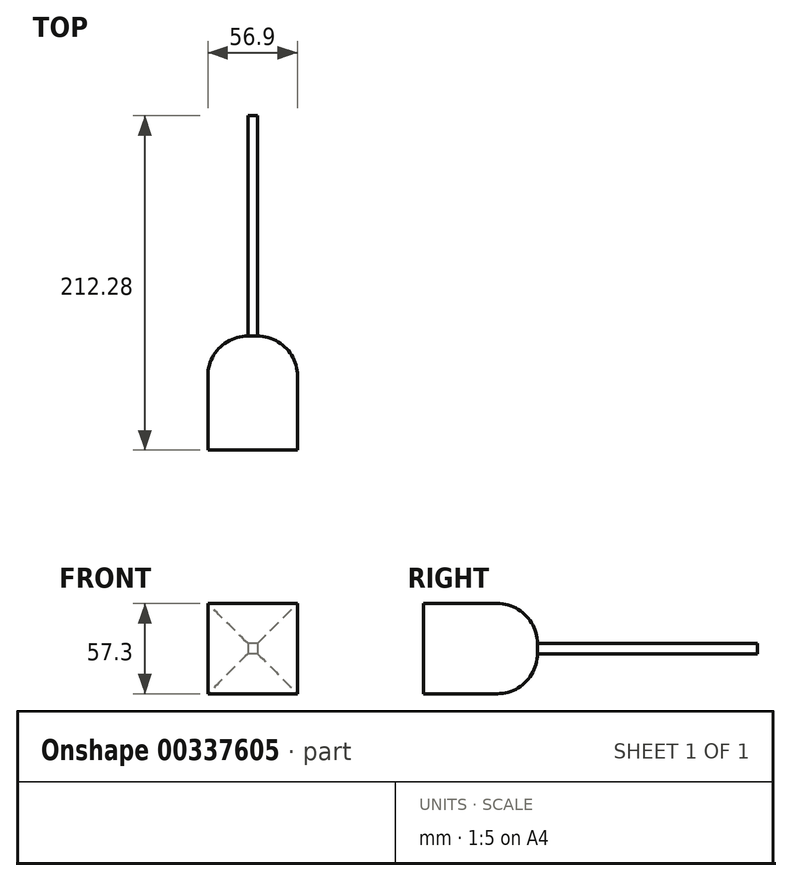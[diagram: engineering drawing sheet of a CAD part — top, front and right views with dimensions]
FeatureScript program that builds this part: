
annotation { "Feature Type Name" : "Feature", "Feature Type Description" : "" }
export const myFeature = defineFeature(function(context is Context, id is Id, definition is map)
    precondition{}
    {
        {
            var Q0;
            Q0=qCreatedBy(makeId("Top.planeOp"),FACE);
            var sketch = newSketch(context, id + "F0", { "sketchPlane" : qUnion([Q0])});
            skLineSegment(sketch, "E0.bottom", {"start": v(0, 0) * mm, "end": v(0, 0) * mm});
            skLineSegment(sketch, "E0.top", {"start": v(0, 0) * mm, "end": v(0, 0) * mm});
            skLineSegment(sketch, "E0.left", {"start": v(0, 0) * mm, "end": v(0, 0) * mm});
            skLineSegment(sketch, "E0.right", {"start": v(0, 0) * mm, "end": v(0, 0) * mm});
            skLineSegment(sketch, "E1.bottom", {"start": v(56.9, -72.43) * mm, "end": v(0, -72.43) * mm});
            skLineSegment(sketch, "E1.top", {"start": v(56.9, 0) * mm, "end": v(0, 0) * mm});
            skLineSegment(sketch, "E1.left", {"start": v(56.9, -72.43) * mm, "end": v(56.9, 0) * mm});
            skLineSegment(sketch, "E1.right", {"start": v(0, -72.43) * mm, "end": v(0, 0) * mm});
            skSolve(sketch);
        }
        {
            var Q0;
            Q0=makeQuery(id+"F0.imprint","IMPRINT",FACE,{"disambiguationData":[TD([[makeQuery(id+"F0.imprint","IMPRINT",EDGE,{"derivedFrom":sQuery(id+"F0.wireOp",EDGE,"E1.bottom")}),-1.0]])]});
            extrude(context, id + "F1", {"entities" : qUnion([Q0]), "endBound" : BoundingType.SYMMETRIC, "depth" : 57.3 * mm});
        }
        {
            var Q0;
            Q0=makeQuery(id+"F1.opExtrude","SWEPT_FACE",FACE,{"disambiguationData":[OSD([sQuery(id+"F0.wireOp",EDGE,"E1.top")])]});
            fillet(context, id + "F2", {"entities" : qUnion([Q0]), "radius" : 25.4 * mm, "tangentPropagation" : true, "allowEdgeOverflow" : false});
        }
        {
            var Q0;
            Q0=makeQuery(id+"F1.opExtrude","SWEPT_FACE",FACE,{"disambiguationData":[OSD([sQuery(id+"F0.wireOp",EDGE,"E1.top")])]});
            extrude(context, id + "F3", {"entities" : qUnion([Q0]), "operationType" : NewBodyOperationType.ADD, "depth" : 139.85 * mm});
        }
    });
